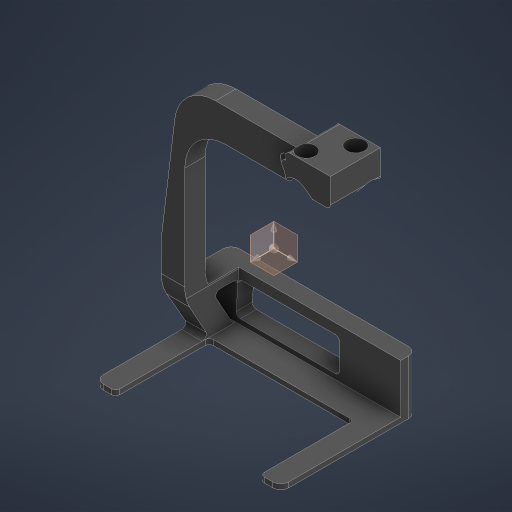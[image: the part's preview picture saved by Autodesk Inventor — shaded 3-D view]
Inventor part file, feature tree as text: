
AUTODESK INVENTOR PART (.ipt)
format: ipt  version: 2024.2 (Build 282272000, 272)  size: 663,552 bytes
history: native  units: in
note: dims shown in document units (in); Inventor stores cm internally (conversion verified against a paired STEP export)
features: reference x31, projected_geometry x23, extrude x21, sketch x14, other x11, fillet x10, chamfer x4, plane x1
ambient origin geometry x8: Origin, YZ Plane, XZ Plane, XY Plane, X Axis, Y Axis, Z Axis, Center Point
bodies: Solid1 (feature_tree)
feature tree (115):
  plane  "Work Plane1"
  extrude  "Extrusion1"  Depth=0.4in
  fillet  "Fillet1"  Radius=0.125in
  chamfer  "Chamfer1"  Distance=0.25in
  sketch  "Sketch3"  dims[d3=0.12in]
  extrude  "Extrusion2"  Depth=0.005in TaperAngle=45.0deg
  sketch  "Sketch4"  dims[d4=0.01in]
  extrude  "Extrusion5"  Depth=1.69in
  sketch  "Sketch5"  dims[d5=0.0625in d6=0.25in d7=0.0in]
  extrude  "Extrusion6"  Depth=2.263in
  extrude  "Extrusion7"  Depth=0.25in
  extrude  "Extrusion8"  Depth=0.5841in
  extrude  "Extrusion9"  Depth=0.3in TaperAngle=0.0deg
  sketch  "Sketch7"  dims[d12=0.0625in d13=0.0in d16=1.69in]
  extrude  "Extrusion10"  Depth=0.5in
  extrude  "Extrusion11"  Depth=0.05in
  fillet  "Fillet6"  [1 undecoded]
  fillet  "Fillet7"  Radius=0.25in
  fillet  "Fillet8"  Radius=0.2865in
  extrude  "Extrusion12"  Depth=0.25in TaperAngle=0.0deg
  extrude  "Extrusion13"  Depth=0.05in
  extrude  "Extrusion14"  TaperAngle=0.0deg  [1 undecoded]
  extrude  "Extrusion15"  Depth=0.05in
  extrude  "Extrusion17"  TaperAngle=0.0deg  [1 undecoded]
  extrude  "Extrusion18"  Depth=0.05in TaperAngle=0.0deg
  extrude  "Extrusion19"  Depth=0.05in
  fillet  "Fillet10"  Radius=0.3313in
  sketch  "Sketch17"  dims[d40=0.5in d41=0.1in d42=0.0in d43=0.0in d44=0.05in d45=0.0in d46=0.0in d47=0.3361in d48=0.0in d49=0.1236in d50=0.3313in d51=0.385in d52=0.6in d53=0.0in d54=0.7in d55=0.0in d56=1.0in d57=0.0in d59=0.125in d60=0.125in d61=0.0in d62=0.125in d63=0.125in d64=45.0deg d67=0.16in d68=0.45in d69=0.0in d70=0.0in d71=2.0in d72=0.0in d73=0.5in d74=0.0in d75=0.05in d76=0.222in d78=0.222in d82=0.015in d83=0.431in d84=0.431in d87=0.1in d88=0.125in d89=45.0deg d90=0.5in d91=0.0in d92=0.15in d93=0.0in d94=0.0in d95=0.0in d96=0.05in d97=0.125in d98=0.125in d99=45.0deg d100=0.075in d101=0.05in d77=0.5in]
  extrude  "Extrusion21"  Depth=0.05in
  extrude  "Extrusion22"  Depth=0.05in TaperAngle=0.0deg
  extrude  "Extrusion23"  Depth=0.05in TaperAngle=0.0deg
  fillet  "Fillet11"  Radius=1.0in
  chamfer  "Chamfer4"  Distance=0.125in
  fillet  "Fillet12"  Radius=0.125in
  fillet  "Fillet13"  Radius=0.125in
  chamfer  "Chamfer3"  Distance=0.16in
  chamfer  "Chamfer2"  Distance=2.0in
  extrude  "Extrusion3"  Depth=0.05in TaperAngle=0.0deg
  extrude  "Extrusion4"  Depth=0.05in
  fillet  "Fillet4"  Radius=0.222in
  fillet  "Fillet5"  Radius=0.222in
  sketch  "Sketch2"  dims[d0=0.005in d1=0.4in d2=0.125in]
  reference  "Reference2"
  reference  "Reference3"
  reference  "Reference4"
  reference  "Reference5"
  reference  "Reference6"
  reference  "Reference7"
  reference  "Reference8"
  reference  "Reference9"
  reference  "Reference10"
  reference  "Reference11"
  reference  "Reference12"
  reference  "Reference13"
  reference  "Reference14"
  reference  "Reference15"
  reference  "Reference16"
  reference  "Reference17"
  reference  "Reference18"
  reference  "Reference19"
  reference  "Reference20"
  reference  "Reference21"
  reference  "Reference22"
  reference  "Reference23"
  reference  "Reference24"
  reference  "Reference25"
  reference  "Reference26"
  projected_geometry  "Projected Loop1"
  reference  "Reference27"
  reference  "Reference28"
  reference  "Reference29"
  reference  "Reference30"
  reference  "Reference31"
  projected_geometry  "Projected Loop2"
  projected_geometry  "Projected Loop3"
  projected_geometry  "Projected Loop4"
  sketch  "Sketch6"  dims[d8=0.5in d9=0.005in d10=0.125in d11=45.0deg]
  projected_geometry  "Projected Loop5"
  projected_geometry  "Projected Loop6"
  projected_geometry  "Projected Loop7"
  projected_geometry  "Projected Loop8"
  sketch  "Sketch8"  dims[d17=2.263in d18=2.263in]
  projected_geometry  "Projected Loop9"
  reference  "Reference32"
  projected_geometry  "Projected Loop10"
  projected_geometry  "Projected Loop11"
  sketch  "Sketch9"  dims[d19=0.25in d20=0.25in]
  projected_geometry  "Projected Loop12"
  sketch  "Sketch10"  dims[d21=0.6528in d22=0.5841in]
  projected_geometry  "Projected Loop13"
  projected_geometry  "Projected Loop14"
  projected_geometry  "Projected Loop15"
  projected_geometry  "Projected Loop16"
  sketch  "Sketch11"  dims[d23=0.25in d24=0.0in d25=0.3in d26=0.0in]
  projected_geometry  "Projected Loop19"
  sketch  "Sketch14"  dims[d27=0.125in d28=0.0in d29=0.5in]
  projected_geometry  "Projected Loop20"
  sketch  "Sketch15"  dims[d30=0.125in d31=0.05in d32=120.0deg d33=0.25in d34=0.2865in d35=0.0in]
  projected_geometry  "Projected Loop21"
  sketch  "Sketch16"  dims[d36=0.0in d37=0.0in d38=0.25in d39=0.0in]
  projected_geometry  "Projected Loop22"
  projected_geometry  "Projected Loop23"
  projected_geometry  "Projected Loop24"
  projected_geometry  "Projected Loop25"
  other  "<userpath>\Documents\School\FallCAD\Bio\Bio.iam"
  other  "Bio.iam"
  other  "Servo HS425BB:1"
  other  "ServoMount:1"
  other  "92095A186_Button Head Hex Drive Screw:1"
  other  "92095A186_Button Head Hex Drive Screw:2"
  other  "90576A102_Medium-Strength Steel Nylon-Insert Locknut:4"
  other  "FrontLinkage:1"
  other  "90576A102_Medium-Strength Steel Nylon-Insert Locknut:2"
  other  "90576A102_Medium-Strength Steel Nylon-Insert Locknut:1"
  other  "Leg_MIR:1"
note: 3 required parameter values undecoded (feature->parameter linkage not recoverable at this tier; creation-order binding heuristic only, values carry confidence <= 0.55)
